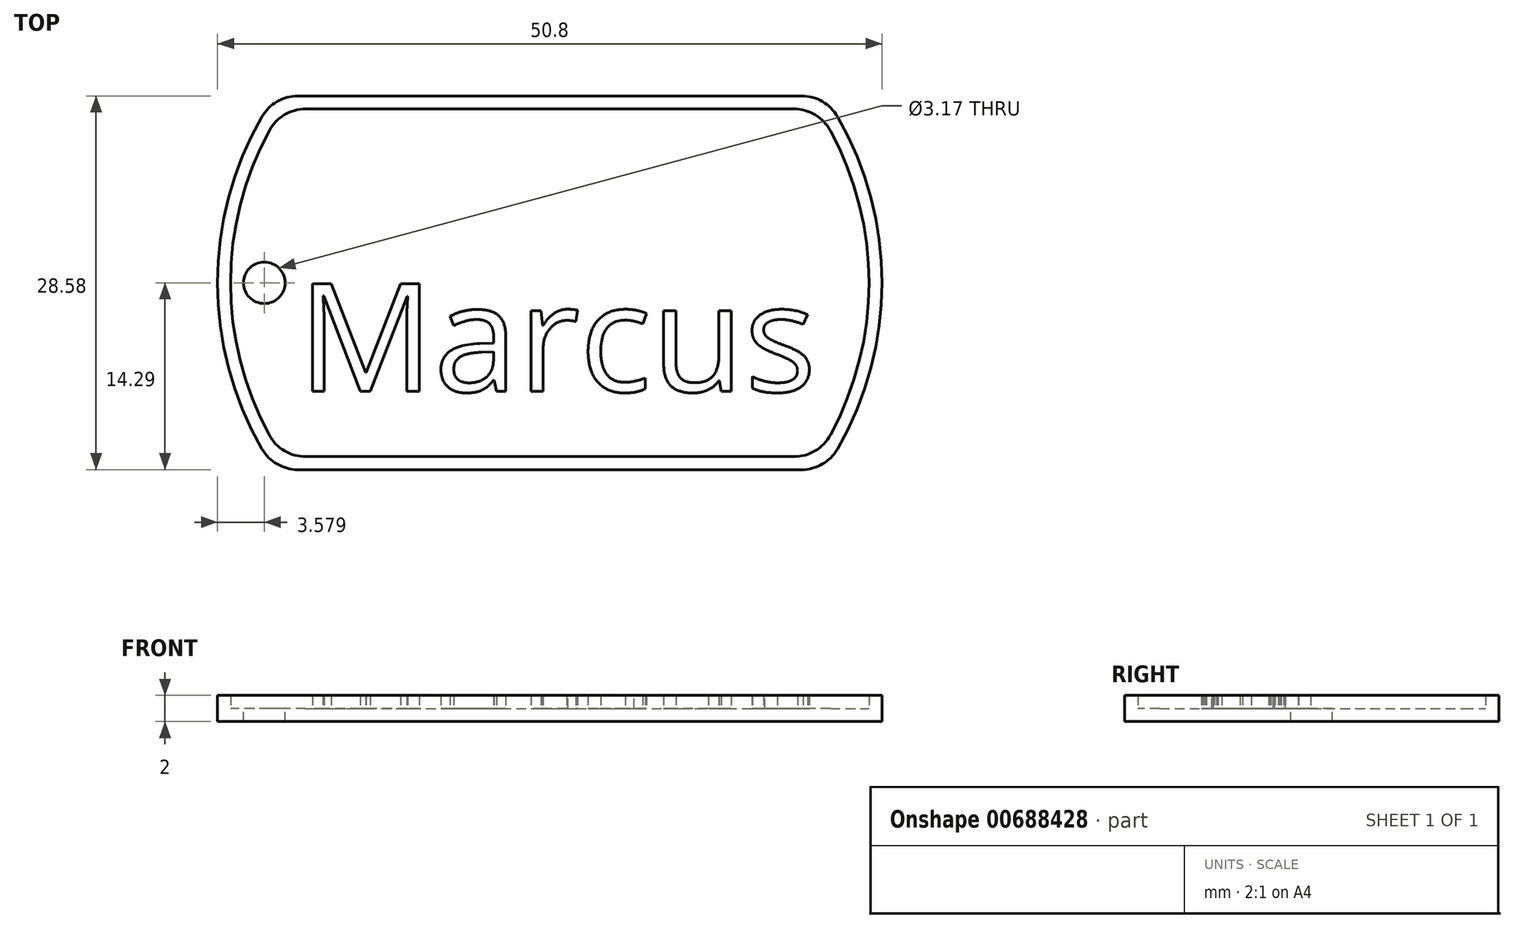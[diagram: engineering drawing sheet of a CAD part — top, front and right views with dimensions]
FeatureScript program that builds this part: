
annotation { "Feature Type Name" : "Feature", "Feature Type Description" : "" }
export const myFeature = defineFeature(function(context is Context, id is Id, definition is map)
    precondition{}
    {
        {
            var Q0;
            Q0=qCreatedBy(makeId("Top.planeOp"),FACE);
            var sketch = newSketch(context, id + "F0", { "sketchPlane" : qUnion([Q0])});
            skArc(sketch, "E0", {"start": v(-22, 12.7) * mm, "mid": v(-25.4, 0) * mm, "end": v(-22, -12.7) * mm});
            skLineSegment(sketch, "E1.top", {"start": v(-19.25, -14.29) * mm, "end": v(19.25, -14.29) * mm});
            skArc(sketch, "E2.trimOffspring", {"start": v(22, -12.7) * mm, "mid": v(25.4, 0) * mm, "end": v(22, 12.7) * mm});
            skLineSegment(sketch, "E3", {"start": v(-19.25, 14.29) * mm, "end": v(19.25, 14.29) * mm});
            skPoint(sketch, "E4.visualSharp", {"position": v(-21, 14.29) * mm});
            skArc(sketch, "E4.filletArc", {"start": v(-19.25, 14.29) * mm, "mid": v(-20.83, 13.86) * mm, "end": v(-22, 12.7) * mm});
            skPoint(sketch, "E5.visualSharp", {"position": v(21, 14.29) * mm});
            skArc(sketch, "E5.filletArc", {"start": v(22, 12.7) * mm, "mid": v(20.83, 13.86) * mm, "end": v(19.25, 14.29) * mm});
            skPoint(sketch, "E6.visualSharp", {"position": v(21, -14.29) * mm});
            skArc(sketch, "E6.filletArc", {"start": v(19.25, -14.29) * mm, "mid": v(20.83, -13.86) * mm, "end": v(22, -12.7) * mm});
            skPoint(sketch, "E7.visualSharp", {"position": v(-21, -14.29) * mm});
            skArc(sketch, "E7.filletArc", {"start": v(-22, -12.7) * mm, "mid": v(-20.83, -13.86) * mm, "end": v(-19.25, -14.29) * mm});
            skSolve(sketch);
        }
        {
            var Q0;
            Q0=makeQuery(id+"F0.imprint","IMPRINT",FACE,{"disambiguationData":[TD([[makeQuery(id+"F0.imprint","IMPRINT",EDGE,{"derivedFrom":sQuery(id+"F0.wireOp",EDGE,"E0")}),1.0]])]});
            extrude(context, id + "F1", {"entities" : qUnion([Q0]), "depth" : 1 * mm, "offsetDistance" : 25.4 * mm});
        }
        {
            var Q0;
            Q0=makeQuery(id+"F1.opExtrude","CAP_FACE",FACE,{"disambiguationData":[OSD([sQuery(id+"F0.wireOp",EDGE,"E0"),sQuery(id+"F0.wireOp",EDGE,"E1.top"),sQuery(id+"F0.wireOp",EDGE,"E2.trimOffspring"),sQuery(id+"F0.wireOp",EDGE,"E3"),sQuery(id+"F0.wireOp",EDGE,"E4.filletArc"),sQuery(id+"F0.wireOp",EDGE,"E5.filletArc"),sQuery(id+"F0.wireOp",EDGE,"E6.filletArc"),sQuery(id+"F0.wireOp",EDGE,"E7.filletArc")])],"isStart":false});
            var sketch = newSketch(context, id + "F2", { "sketchPlane" : qUnion([Q0])});
            skLineSegment(sketch, "E8.0", {"start": v(-18.66, 13.29) * mm, "end": v(18.66, 13.29) * mm});
            skArc(sketch, "E8.1", {"start": v(-21.45, 11.63) * mm, "mid": v(-24.4, 0) * mm, "end": v(-21.45, -11.63) * mm});
            skLineSegment(sketch, "E8.2", {"start": v(-18.66, -13.29) * mm, "end": v(18.66, -13.29) * mm});
            skArc(sketch, "E8.3", {"start": v(21.45, -11.63) * mm, "mid": v(24.4, 0) * mm, "end": v(21.45, 11.63) * mm});
            skPoint(sketch, "E9.visualSharp", {"position": v(-20.46, 13.29) * mm});
            skArc(sketch, "E9.filletArc", {"start": v(-18.66, 13.29) * mm, "mid": v(-20.29, 12.84) * mm, "end": v(-21.45, 11.63) * mm});
            skPoint(sketch, "E10.visualSharp", {"position": v(20.46, 13.29) * mm});
            skArc(sketch, "E10.filletArc", {"start": v(21.45, 11.63) * mm, "mid": v(20.29, 12.84) * mm, "end": v(18.66, 13.29) * mm});
            skPoint(sketch, "E11.visualSharp", {"position": v(20.46, -13.29) * mm});
            skArc(sketch, "E11.filletArc", {"start": v(18.66, -13.29) * mm, "mid": v(20.29, -12.84) * mm, "end": v(21.45, -11.63) * mm});
            skPoint(sketch, "E12.visualSharp", {"position": v(-20.46, -13.29) * mm});
            skArc(sketch, "E12.filletArc", {"start": v(-21.45, -11.63) * mm, "mid": v(-20.29, -12.84) * mm, "end": v(-18.66, -13.29) * mm});
            skLineSegment(sketch, "E13.0", {"start": v(-19.25, 14.29) * mm, "end": v(19.25, 14.29) * mm});
            skArc(sketch, "E13.1", {"start": v(-22, 12.7) * mm, "mid": v(-25.4, 0) * mm, "end": v(-22, -12.7) * mm});
            skLineSegment(sketch, "E13.2", {"start": v(-19.25, -14.29) * mm, "end": v(19.25, -14.29) * mm});
            skArc(sketch, "E13.3", {"start": v(22, -12.7) * mm, "mid": v(25.4, 0) * mm, "end": v(22, 12.7) * mm});
            skPoint(sketch, "E14.visualSharp", {"position": v(-21, -14.29) * mm});
            skArc(sketch, "E14.filletArc", {"start": v(-22, -12.7) * mm, "mid": v(-20.83, -13.86) * mm, "end": v(-19.25, -14.29) * mm});
            skPoint(sketch, "E15.visualSharp", {"position": v(21, -14.29) * mm});
            skArc(sketch, "E15.filletArc", {"start": v(19.25, -14.29) * mm, "mid": v(20.83, -13.86) * mm, "end": v(22, -12.7) * mm});
            skPoint(sketch, "E16.visualSharp", {"position": v(21, 14.29) * mm});
            skArc(sketch, "E16.filletArc", {"start": v(22, 12.7) * mm, "mid": v(20.83, 13.86) * mm, "end": v(19.25, 14.29) * mm});
            skPoint(sketch, "E17.visualSharp", {"position": v(-21, 14.29) * mm});
            skArc(sketch, "E17.filletArc", {"start": v(-19.25, 14.29) * mm, "mid": v(-20.83, 13.86) * mm, "end": v(-22, 12.7) * mm});
            skSolve(sketch);
        }
        {
            var Q0;
            Q0=makeQuery(id+"F2.imprint","IMPRINT",FACE,{"disambiguationData":[TD([[makeQuery(id+"F2.imprint","IMPRINT",EDGE,{"derivedFrom":sQuery(id+"F2.wireOp",EDGE,"E8.0")}),1.0]])]});
            extrude(context, id + "F3", {"entities" : qUnion([Q0]), "operationType" : NewBodyOperationType.ADD, "depth" : 1 * mm, "offsetDistance" : 25.4 * mm});
        }
        {
            var Q0;
            Q0=makeQuery(id+"F1.opExtrude","CAP_FACE",FACE,{"disambiguationData":[OSD([sQuery(id+"F0.wireOp",EDGE,"E0"),sQuery(id+"F0.wireOp",EDGE,"E1.top"),sQuery(id+"F0.wireOp",EDGE,"E2.trimOffspring"),sQuery(id+"F0.wireOp",EDGE,"E3"),sQuery(id+"F0.wireOp",EDGE,"E4.filletArc"),sQuery(id+"F0.wireOp",EDGE,"E5.filletArc"),sQuery(id+"F0.wireOp",EDGE,"E6.filletArc"),sQuery(id+"F0.wireOp",EDGE,"E7.filletArc")])],"isStart":false});
            var sketch = newSketch(context, id + "F4", { "sketchPlane" : qUnion([Q0])});
            skCircle(sketch, "E18", {"center": v(-21.82, 0) * mm, "radius": 1.59 * mm});
            skSolve(sketch);
        }
        {
            var Q0;
            Q0=makeQuery(id+"F4.imprint","IMPRINT",FACE,{"disambiguationData":[TD([[makeQuery(id+"F4.imprint","IMPRINT",EDGE,{"derivedFrom":sQuery(id+"F4.wireOp",EDGE,"E18")}),1.0]])]});
            extrude(context, id + "F5", {"entities" : qUnion([Q0]), "operationType" : NewBodyOperationType.REMOVE, "oppositeDirection" : true, "depth" : 1 * mm, "offsetDistance" : 25.4 * mm});
        }
        {
            var Q0;
            Q0=makeQuery(id+"F2.imprint","IMPRINT",FACE,{"disambiguationData":[TD([[makeQuery(id+"F2.imprint","IMPRINT",EDGE,{"derivedFrom":sQuery(id+"F2.wireOp",EDGE,"E8.0")}),-1.0]])]});
            var sketch = newSketch(context, id + "F6", { "sketchPlane" : qUnion([Q0])});
            skText(sketch, "E19", { "text": "Marcus", "fontName": "OpenSans-Regular.ttf"});
            const initialGuessF6  = {"E19": [-0.01927, -0.00831, 1, 0, 0.00831]};
            skSetInitialGuess(sketch, initialGuessF6);
            skSolve(sketch);
        }
        {
            var Q0;
            Q0 = qSketchRegion(id + "F6", true);
            extrude(context, id + "F7", {"entities" : qUnion([Q0]), "operationType" : NewBodyOperationType.ADD, "depth" : 1 * mm, "offsetDistance" : 25.4 * mm});
        }
    });
